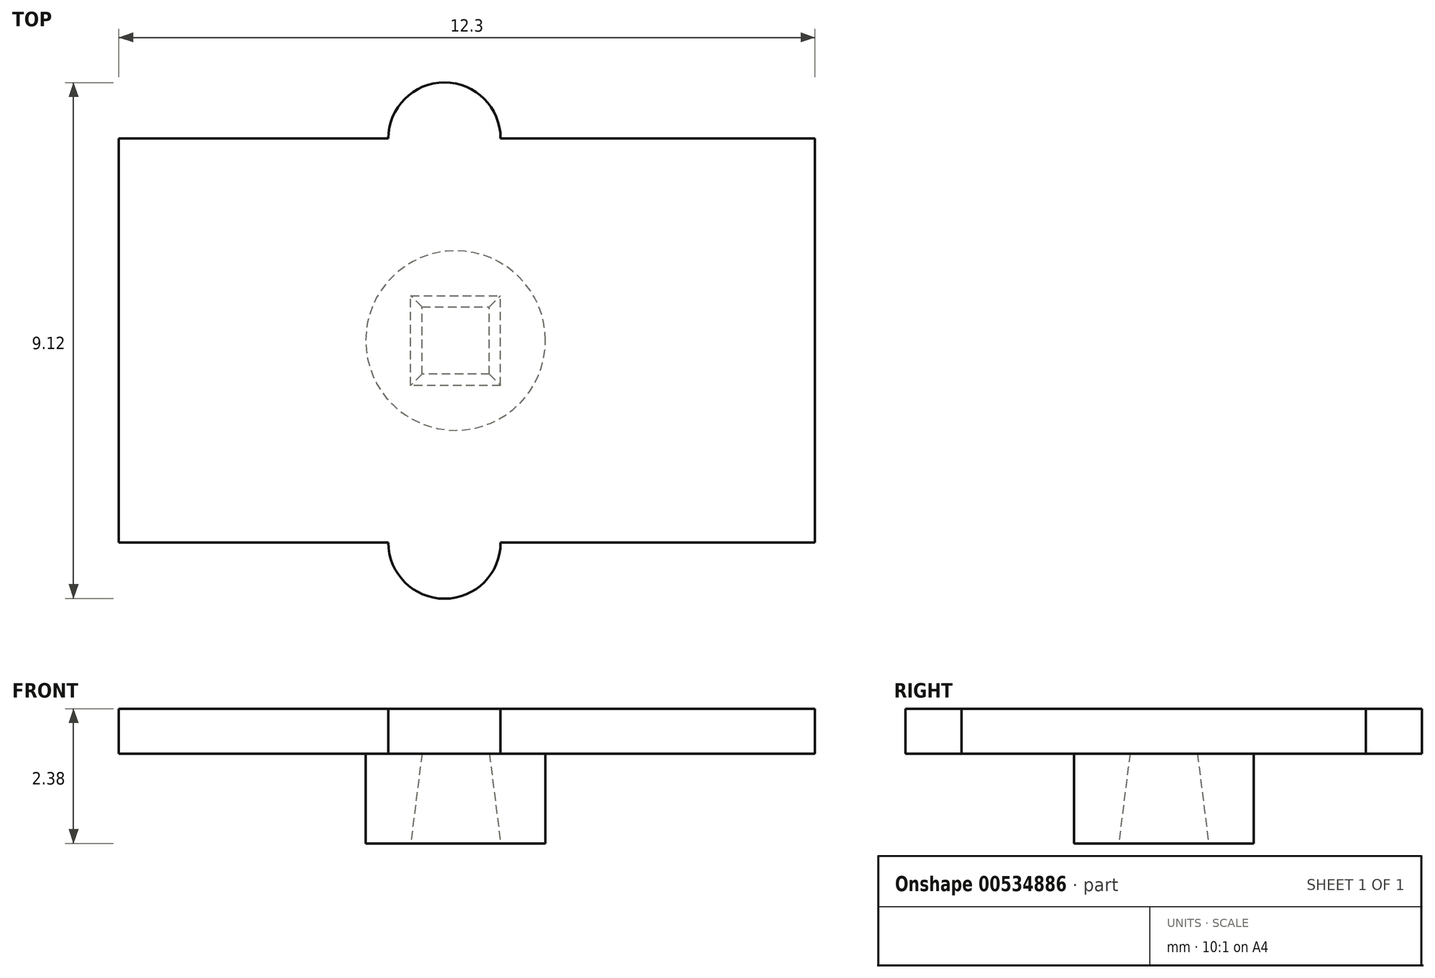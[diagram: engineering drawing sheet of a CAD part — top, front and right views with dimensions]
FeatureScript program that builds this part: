
annotation { "Feature Type Name" : "Feature", "Feature Type Description" : "" }
export const myFeature = defineFeature(function(context is Context, id is Id, definition is map)
    precondition{}
    {
        {
            var Q0;
            Q0=qCreatedBy(makeId("Top.planeOp"),FACE);
            var sketch = newSketch(context, id + "F0", { "sketchPlane" : qUnion([Q0])});
            skCircle(sketch, "E0", {"center": v(0, 0) * mm, "radius": 1.59 * mm});
            skSolve(sketch);
        }
        {
            var Q0;
            Q0 = qSketchRegion(id + "F0", true);
            extrude(context, id + "F1", {"entities" : qUnion([Q0]), "depth" : 1.59 * mm, "offsetDistance" : 25.4 * mm});
        }
        {
            var Q0;
            Q0=makeQuery(id+"F1.opExtrude","CAP_FACE",FACE,{"disambiguationData":[OSD([sQuery(id+"F0.wireOp",EDGE,"E0"),sQuery(id+"F0.wireOp",EDGE,"MDIm75e0-zWpY-x6Is-moMT-37JhcSPX7jKy"),sQuery(id+"F0.wireOp",EDGE,"OrDAee1F-gJgk-GVKq-04dE-2IDSRpdsH9WQ"),sQuery(id+"F0.wireOp",EDGE,"LkNqx7aF-VXLt-TfgJ-F0Ho-SwGb08xpQ5Qp"),sQuery(id+"F0.wireOp",EDGE,"Xgk9G2vi-4R0v-lAy6-mJPd-sz3B3CfKhcv3")])],"isStart":false});
            var sketch = newSketch(context, id + "F2", { "sketchPlane" : qUnion([Q0])});
            skLineSegment(sketch, "E1", {"start": v(0.6, -0.6) * mm, "end": v(-0.6, -0.6) * mm});
            skLineSegment(sketch, "E2", {"start": v(-0.6, -0.6) * mm, "end": v(-0.6, 0.6) * mm});
            skLineSegment(sketch, "E3", {"start": v(-0.6, 0.6) * mm, "end": v(0.6, 0.6) * mm});
            skLineSegment(sketch, "E4", {"start": v(0.6, -0.6) * mm, "end": v(0.6, 0.6) * mm});
            skSolve(sketch);
        }
        {
            var Q0;
            Q0=makeQuery(id+"F1.opExtrude","CAP_FACE",FACE,{"disambiguationData":[OSD([sQuery(id+"F0.wireOp",EDGE,"E0")])],"isStart":true});
            var sketch = newSketch(context, id + "F3", { "sketchPlane" : qUnion([Q0])});
            skLineSegment(sketch, "E5", {"start": v(0.8, 0.8) * mm, "end": v(-0.8, 0.8) * mm});
            skLineSegment(sketch, "E6", {"start": v(-0.8, 0.8) * mm, "end": v(-0.8, -0.8) * mm});
            skLineSegment(sketch, "E7", {"start": v(-0.8, -0.8) * mm, "end": v(0.8, -0.8) * mm});
            skLineSegment(sketch, "E8", {"start": v(0.8, 0.8) * mm, "end": v(0.8, -0.8) * mm});
            skSolve(sketch);
        }
        {
            var Q1;
            Q1 = qSketchRegion(id + "F2", true);
            var Q2;
            Q2 = qSketchRegion(id + "F3", true);
            loft(context, id + "F4", {"operationType" : NewBodyOperationType.REMOVE, "sheetProfilesArray" : [{ "sheetProfileEntities" : qUnion([Q1]) }, { "sheetProfileEntities" : qUnion([Q2]) }]});
        }
        {
            var Q0;
            Q0=makeQuery(id+"F1.opExtrude","CAP_FACE",FACE,{"disambiguationData":[OSD([sQuery(id+"F0.wireOp",EDGE,"E0")])],"isStart":false});
            var sketch = newSketch(context, id + "F5", { "sketchPlane" : qUnion([Q0])});
            skLineSegment(sketch, "E9", {"start": v(-5.95, -3.57) * mm, "end": v(-1.2, -3.57) * mm});
            skLineSegment(sketch, "E10", {"start": v(-5.95, 3.57) * mm, "end": v(-1.2, 3.57) * mm});
            skLineSegment(sketch, "E11", {"start": v(6.35, -3.57) * mm, "end": v(6.35, 3.57) * mm});
            skLineSegment(sketch, "E12", {"start": v(-5.95, -3.57) * mm, "end": v(-5.95, 3.57) * mm});
            skArc(sketch, "E13", {"start": v(-1.2, -3.57) * mm, "mid": v(-0.2, -4.56) * mm, "end": v(0.8, -3.57) * mm});
            skArc(sketch, "E14", {"start": v(0.8, 3.57) * mm, "mid": v(-0.2, 4.56) * mm, "end": v(-1.2, 3.57) * mm});
            skLineSegment(sketch, "E15.trimOffspring", {"start": v(0.8, -3.57) * mm, "end": v(6.35, -3.57) * mm});
            skLineSegment(sketch, "E16.trimOffspring", {"start": v(0.8, 3.57) * mm, "end": v(6.35, 3.57) * mm});
            skSolve(sketch);
        }
        {
            var Q0;
            Q0 = qSketchRegion(id + "F5", true);
            extrude(context, id + "F6", {"entities" : qUnion([Q0]), "operationType" : NewBodyOperationType.ADD, "depth" : 0.8 * mm, "offsetDistance" : 25.4 * mm});
        }
    });
